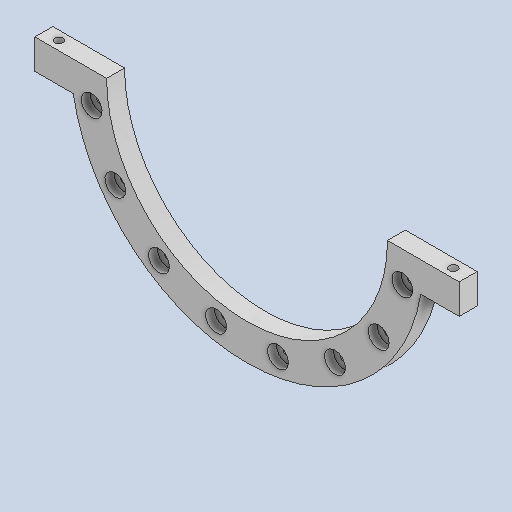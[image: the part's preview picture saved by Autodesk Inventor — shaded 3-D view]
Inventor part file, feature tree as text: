
AUTODESK INVENTOR PART (.ipt)
format: ipt  version: 2024.2 (Build 282272000, 272)  size: 382,464 bytes
history: native  units: mm
features: sketch x4, extrude x2, hole x2, mirror x2, other x2, fillet x1, pattern_circular x1
ambient origin geometry x8: Origin, YZ Plane, XZ Plane, XY Plane, X Axis, Y Axis, Z Axis, Center Point
bodies: Solid1 (feature_tree)
feature tree (14):
  extrude  "Extrusion1"  Depth=30.0mm
  sketch  "Sketch4"  dims[d27=265.0mm d35=1.963495mm]
  sketch  "Sketch7"  dims[d36=60.0mm d40=60.0mm d41=50.0mm]
  fillet  "Fillet1"  Radius=80.0mm
  hole  "Hole1"  [1 undecoded]
  hole  "Hole2"  [1 undecoded]
  pattern_circular  "Circular Pattern4"  Count=5  [1 undecoded]
  mirror  "Mirror1"
  extrude  "Extrusion8"  Depth=10.0mm
  mirror  "Mirror2"
  other  "A-Side Definition"
  sketch  "Sketch1"  dims[d2=30.0mm d3=0.0mm d13=530.0mm d26=80.0mm]
  sketch  "Sketch9"  dims[d42=25.0mm d45=10.0mm d46=14.0mm d47=32.0mm d48=24.0mm d49=15.0mm d50=90.0deg d51=8.0mm d52=20.594885mm d53=13.0mm d54=6.0mm d55=35.0mm d56=15.0mm d57=90.0deg d58=8.0mm d59=20.594885mm d60=90.0mm d61=180.0deg d70=25.0mm d71=14.0mm d72=0.0mm d73=0.0mm d63=1.0mm d64=1.0mm d65=1.0mm d66=0.15mm d67=0.25mm d68=0.375mm d69=14.3117mm d74=0.375mm]
  other  "Definition1"
note: 3 required parameter values undecoded (feature->parameter linkage not recoverable at this tier; creation-order binding heuristic only, values carry confidence <= 0.55)
